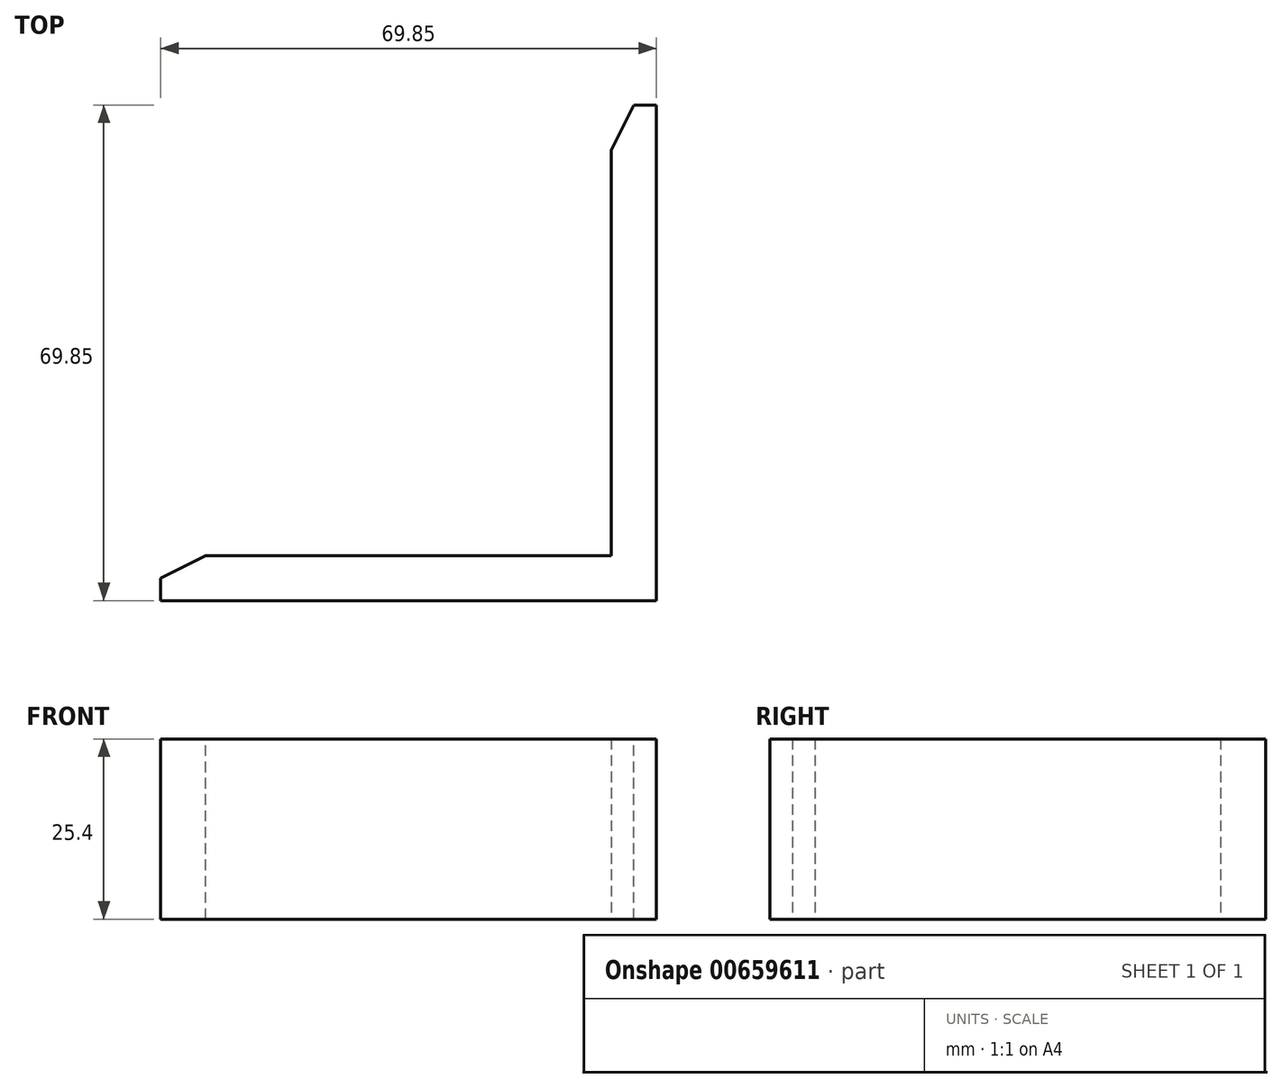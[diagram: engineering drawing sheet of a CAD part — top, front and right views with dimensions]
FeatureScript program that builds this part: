
annotation { "Feature Type Name" : "Feature", "Feature Type Description" : "" }
export const myFeature = defineFeature(function(context is Context, id is Id, definition is map)
    precondition{}
    {
        {
            var Q0;
            Q0=qCreatedBy(makeId("Top.planeOp"),FACE);
            var sketch = newSketch(context, id + "F0", { "sketchPlane" : qUnion([Q0])});
            skLineSegment(sketch, "E0.bottom", {"start": v(25.4, -25.4) * mm, "end": v(-25.4, -25.4) * mm});
            skLineSegment(sketch, "E0.top", {"start": v(25.4, 25.4) * mm, "end": v(-25.4, 25.4) * mm});
            skLineSegment(sketch, "E0.left", {"start": v(25.4, -25.4) * mm, "end": v(25.4, 25.4) * mm});
            skLineSegment(sketch, "E0.right", {"start": v(-25.4, -25.4) * mm, "end": v(-25.4, 25.4) * mm});
            skPoint(sketch, "E0.middle", {"position": v(0, 0) * mm});
            skLineSegment(sketch, "E1", {"start": v(-25.4, -25.4) * mm, "end": v(-31.75, -25.4) * mm});
            skLineSegment(sketch, "E2", {"start": v(-31.75, -25.4) * mm, "end": v(-31.75, -31.75) * mm});
            skLineSegment(sketch, "E3", {"start": v(-31.75, -31.75) * mm, "end": v(31.75, -31.75) * mm});
            skLineSegment(sketch, "E4", {"start": v(31.75, -31.75) * mm, "end": v(31.75, 31.75) * mm});
            skLineSegment(sketch, "E5", {"start": v(31.75, 31.75) * mm, "end": v(25.4, 31.75) * mm});
            skLineSegment(sketch, "E6", {"start": v(25.4, 31.75) * mm, "end": v(25.4, 25.4) * mm});
            skLineSegment(sketch, "E7.bottom", {"start": v(-31.75, -25.4) * mm, "end": v(-31.75, -25.4) * mm});
            skLineSegment(sketch, "E7.top", {"start": v(-31.75, -25.4) * mm, "end": v(-31.75, -25.4) * mm});
            skLineSegment(sketch, "E7.left", {"start": v(-31.75, -25.4) * mm, "end": v(-31.75, -25.4) * mm});
            skLineSegment(sketch, "E7.right", {"start": v(-31.75, -25.4) * mm, "end": v(-31.75, -25.4) * mm});
            skSolve(sketch);
        }
        {
            var Q0;
            Q0=makeQuery(id+"F0.imprint","IMPRINT",FACE,{"disambiguationData":[TD([[makeQuery(id+"F0.imprint","IMPRINT",EDGE,{"derivedFrom":sQuery(id+"F0.wireOp",EDGE,"E0.bottom")}),1.0]])]});
            extrude(context, id + "F1", {"entities" : qUnion([Q0]), "depth" : 25.4 * mm, "offsetDistance" : 25.4 * mm});
        }
        {
            var Q0;
            Q0=makeQuery(id+"F1.opExtrude","SWEPT_FACE",FACE,{"disambiguationData":[OSD([sQuery(id+"F0.wireOp",EDGE,"E2")])]});
            extrude(context, id + "F2", {"entities" : qUnion([Q0]), "operationType" : NewBodyOperationType.ADD, "depth" : 6.35 * mm, "offsetDistance" : 25.4 * mm});
        }
        {
            var Q0;
            Q0=makeQuery(id+"F1.opExtrude","SWEPT_FACE",FACE,{"disambiguationData":[OSD([sQuery(id+"F0.wireOp",EDGE,"E5")])]});
            extrude(context, id + "F3", {"entities" : qUnion([Q0]), "operationType" : NewBodyOperationType.ADD, "depth" : 6.35 * mm, "offsetDistance" : 25.4 * mm});
        }
        {
            var Q0;
            Q0=makeQuery(id+"F2.opExtrude","CAP_EDGE",EDGE,{"disambiguationData":[OSD([sQuery(id+"F0.wireOp",EDGE,"E1"),sQuery(id+"F0.wireOp",EDGE,"E2")])],"isStart":false});
            chamfer(context, id + "F4", {"entities" : qUnion([Q0]), "chamferType" : ChamferType.TWO_OFFSETS, "width1" : 3.17 * mm, "oppositeDirection" : false, "width2" : 6.35 * mm, "tangentPropagation" : true});
        }
        {
            var Q0;
            Q0=makeQuery(id+"F3.opExtrude","CAP_EDGE",EDGE,{"disambiguationData":[OSD([sQuery(id+"F0.wireOp",EDGE,"E5"),sQuery(id+"F0.wireOp",EDGE,"E6")])],"isStart":false});
            chamfer(context, id + "F5", {"entities" : qUnion([Q0]), "chamferType" : ChamferType.TWO_OFFSETS, "width1" : 6.35 * mm, "oppositeDirection" : false, "width2" : 3.17 * mm, "tangentPropagation" : true});
        }
    });
